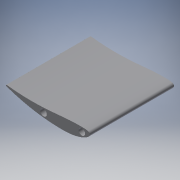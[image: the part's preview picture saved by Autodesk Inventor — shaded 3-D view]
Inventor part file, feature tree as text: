
AUTODESK INVENTOR PART (.ipt)
format: ipt  version: 2018 (Build 220112000, 112)  size: 314,368 bytes
history: native  units: mm
features: other x6, extrude x4, sketch x4, reference x4, projected_geometry x2
ambient origin geometry x8: Origin, YZ Plane, XZ Plane, XY Plane, X Axis, Y Axis, Z Axis, Center Point
bodies: Body1 (feature_tree)
feature tree (20):
  extrude  "押し出し1"  Depth=250.0mm TaperAngle=0.0deg
  other  "作業平面1"
  extrude  "押し出し4"  Depth=225.0mm TaperAngle=0.0deg
  extrude  "押し出し5"  Depth=10.0mm TaperAngle=0.0deg
  extrude  "押し出し6"  Depth=10.0mm TaperAngle=0.0deg
  sketch  "スケッチ1"
  projected_geometry  "投影ループ1"
  sketch  "スケッチ4"
  reference  "参照3"
  reference  "参照4"
  sketch  "スケッチ5"
  projected_geometry  "投影ループ2"
  sketch  "スケッチ6"
  reference  "参照5"
  reference  "参照6"
  other  "<userpath>\Documents\Inventor\Aero\KS-15\Fr.wing\Fr.wing_assy.iam"
  other  "Fr.wing_assy.iam"
  other  "endplate_ver2:2"
  other  "Part1:1"
  other  "newsubflap_top1:1"
